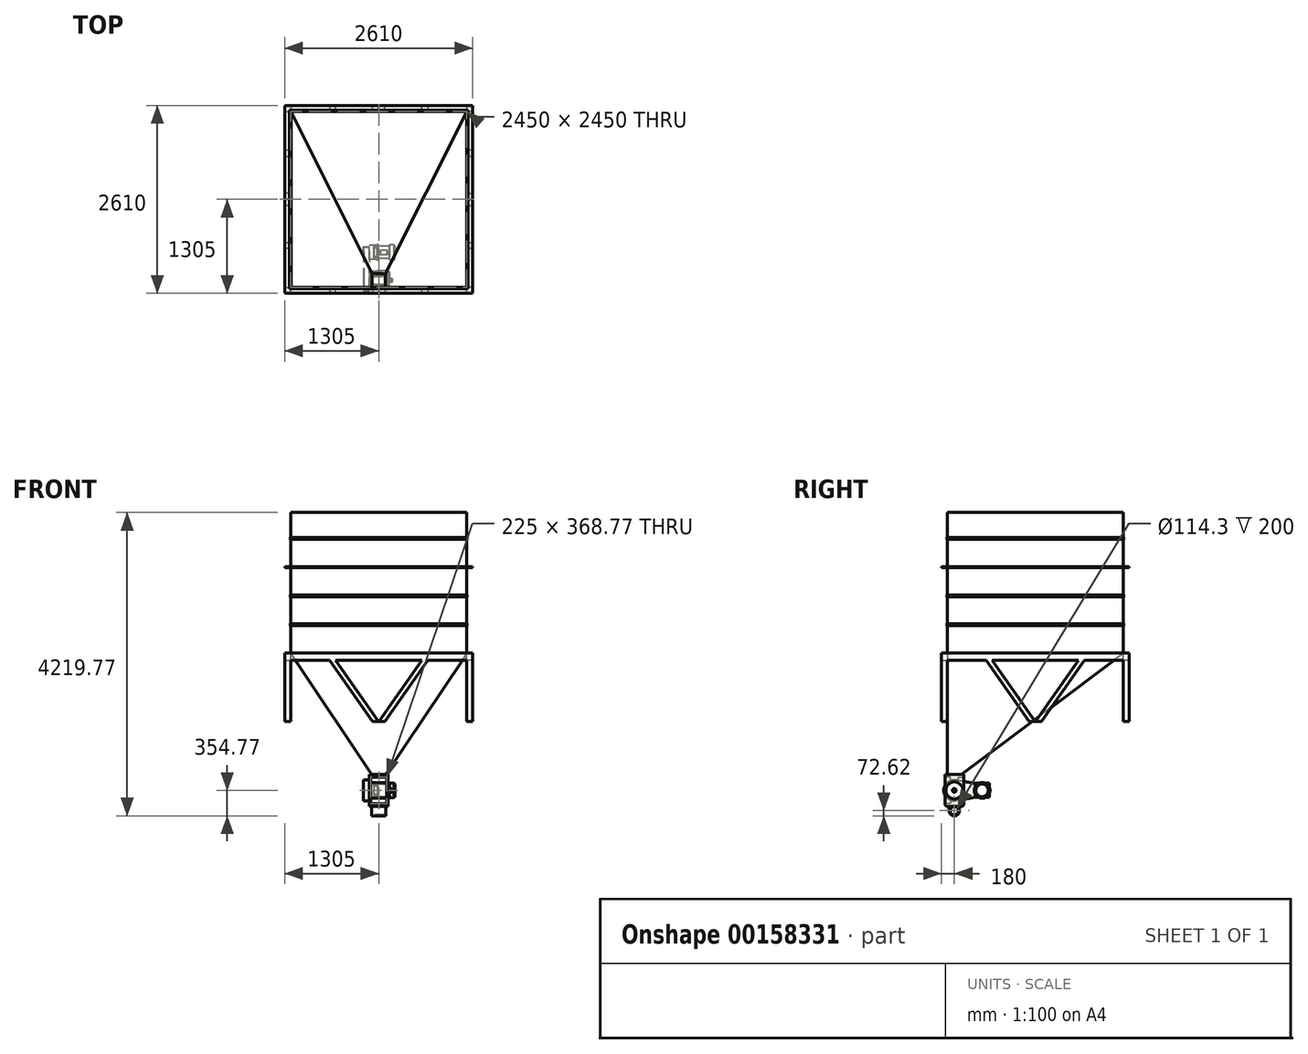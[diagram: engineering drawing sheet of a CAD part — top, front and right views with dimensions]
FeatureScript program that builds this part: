
annotation { "Feature Type Name" : "Feature", "Feature Type Description" : "" }
export const myFeature = defineFeature(function(context is Context, id is Id, definition is map)
    precondition{}
    {
        {
            var Q0;
            Q0=qCreatedBy(makeId("Top.planeOp"),FACE);
            var sketch = newSketch(context, id + "F0", { "sketchPlane" : qUnion([Q0])});
            skLineSegment(sketch, "E0.bottom", {"start": v(-1225, 1225) * mm, "end": v(1225, 1225) * mm});
            skLineSegment(sketch, "E0.top", {"start": v(-1225, -1225) * mm, "end": v(1225, -1225) * mm});
            skLineSegment(sketch, "E0.left", {"start": v(-1225, 1225) * mm, "end": v(-1225, -1225) * mm});
            skLineSegment(sketch, "E0.right", {"start": v(1225, 1225) * mm, "end": v(1225, -1225) * mm});
            skPoint(sketch, "E0.middle", {"position": v(0, 0) * mm});
            skSolve(sketch);
        }
        {
            var Q0;
            Q0=makeQuery(id+"F0.imprint","IMPRINT",FACE,{"disambiguationData":[TD([[makeQuery(id+"F0.imprint","IMPRINT",EDGE,{"derivedFrom":sQuery(id+"F0.wireOp",EDGE,"E0.bottom")}),-1.0]])]});
            extrude(context, id + "F1", {"entities" : qUnion([Q0]), "depth" : 2400 * mm});
        }
        {
            var Q0;
            Q0=makeQuery(id+"F1.opExtrude","CAP_FACE",FACE,{"disambiguationData":[OSD([sQuery(id+"F0.wireOp",EDGE,"E0.bottom"),sQuery(id+"F0.wireOp",EDGE,"E0.top"),sQuery(id+"F0.wireOp",EDGE,"E0.left"),sQuery(id+"F0.wireOp",EDGE,"E0.right")])],"isStart":true});
            cPlane(context, id + "F2", {"entities" : qUnion([Q0]), "cplaneType" : CPlaneType.OFFSET, "offset" : 1680 * mm, "width" : 150 * mm, "height" : 150 * mm});
        }
        {
            var Q0;
            Q0=qCreatedBy(id+"F2.planeOp",FACE);
            var sketch = newSketch(context, id + "F3", { "sketchPlane" : qUnion([Q0])});
            skLineSegment(sketch, "E1.bottom", {"start": v(-100, 1225) * mm, "end": v(100, 1225) * mm});
            skLineSegment(sketch, "E1.top", {"start": v(-100, 1025) * mm, "end": v(100, 1025) * mm});
            skLineSegment(sketch, "E1.left", {"start": v(100, 1225) * mm, "end": v(100, 1025) * mm});
            skLineSegment(sketch, "E1.right", {"start": v(-100, 1225) * mm, "end": v(-100, 1025) * mm});
            skPoint(sketch, "E2", {"position": v(0, 1225) * mm});
            skSolve(sketch);
        }
        {
            var Q1;
            Q1=makeQuery(id+"F1.opExtrude","CAP_FACE",FACE,{"disambiguationData":[OSD([sQuery(id+"F0.wireOp",EDGE,"E0.bottom"),sQuery(id+"F0.wireOp",EDGE,"E0.top"),sQuery(id+"F0.wireOp",EDGE,"E0.left"),sQuery(id+"F0.wireOp",EDGE,"E0.right")])],"isStart":true});
            var Q2;
            Q2=makeQuery(id+"F3.imprint","IMPRINT",FACE,{"disambiguationData":[TD([[makeQuery(id+"F3.imprint","IMPRINT",EDGE,{"derivedFrom":sQuery(id+"F3.wireOp",EDGE,"E1.bottom")}),-1.0]])]});
            loft(context, id + "F4", {"operationType" : NewBodyOperationType.ADD, "sheetProfilesArray" : [{ "sheetProfileEntities" : qUnion([Q1]) }, { "sheetProfileEntities" : qUnion([Q2]) }]});
        }
        {
            var Q0;
            Q0=makeQuery(id+"F1.opExtrude","CAP_FACE",FACE,{"disambiguationData":[OSD([sQuery(id+"F0.wireOp",EDGE,"E0.bottom"),sQuery(id+"F0.wireOp",EDGE,"E0.top"),sQuery(id+"F0.wireOp",EDGE,"E0.left"),sQuery(id+"F0.wireOp",EDGE,"E0.right")])],"isStart":false});
            extrude(context, id + "F5", {"entities" : qUnion([Q0]), "depth" : 400 * mm});
        }
        {
            var Q0;
            Q0=makeQuery(id+"F5.opExtrude","CAP_FACE",FACE,{"disambiguationData":[OSD([sQuery(id+"F0.wireOp",EDGE,"E0.bottom"),sQuery(id+"F0.wireOp",EDGE,"E0.top"),sQuery(id+"F0.wireOp",EDGE,"E0.left"),sQuery(id+"F0.wireOp",EDGE,"E0.right")])],"isStart":false});
            extrude(context, id + "F6", {"entities" : qUnion([Q0]), "depth" : 400 * mm});
        }
        {
            var Q0;
            Q0=makeQuery(id+"F1.opExtrude","CAP_FACE",FACE,{"disambiguationData":[OSD([sQuery(id+"F0.wireOp",EDGE,"E0.bottom"),sQuery(id+"F0.wireOp",EDGE,"E0.top"),sQuery(id+"F0.wireOp",EDGE,"E0.left"),sQuery(id+"F0.wireOp",EDGE,"E0.right")])],"isStart":false});
            var Q1;
            Q1=makeQuery(id+"F4.opLoft","CAP_FACE",FACE,{"disambiguationData":[OSD([makeQuery(id+"F3.imprint","IMPRINT",FACE,{"disambiguationData":[TD([[makeQuery(id+"F3.imprint","IMPRINT",EDGE,{"derivedFrom":sQuery(id+"F3.wireOp",EDGE,"E1.bottom")}),-1.0]])]})])],"isStart":true});
            shell(context, id + "F7", {"entities" : qUnion([Q0, Q1]), "thickness" : 5 * mm});
        }
        {
            var Q0;
            Q0=makeQuery(id+"F1.opExtrude","CAP_FACE",FACE,{"disambiguationData":[OSD([sQuery(id+"F0.wireOp",EDGE,"E0.bottom"),sQuery(id+"F0.wireOp",EDGE,"E0.top"),sQuery(id+"F0.wireOp",EDGE,"E0.left"),sQuery(id+"F0.wireOp",EDGE,"E0.right")])],"isStart":false});
            cPlane(context, id + "F8", {"entities" : qUnion([Q0]), "cplaneType" : CPlaneType.OFFSET, "offset" : 1200 * mm, "oppositeDirection" : true, "width" : 150 * mm, "height" : 150 * mm});
        }
        {
            var Q0;
            Q0=qCreatedBy(id+"F8.planeOp",FACE);
            var sketch = newSketch(context, id + "F9", { "sketchPlane" : qUnion([Q0])});
            skLineSegment(sketch, "E3.bottom", {"start": v(-1305, 1305) * mm, "end": v(1305, 1305) * mm});
            skLineSegment(sketch, "E3.top", {"start": v(-1305, -1305) * mm, "end": v(1305, -1305) * mm});
            skLineSegment(sketch, "E3.left", {"start": v(-1305, 1305) * mm, "end": v(-1305, -1305) * mm});
            skLineSegment(sketch, "E3.right", {"start": v(1305, 1305) * mm, "end": v(1305, -1305) * mm});
            skPoint(sketch, "E3.middle", {"position": v(0, 0) * mm});
            skLineSegment(sketch, "E4.0", {"start": v(-1225, 1225) * mm, "end": v(-1225, -1225) * mm});
            skLineSegment(sketch, "E4.1", {"start": v(-1225, 1225) * mm, "end": v(1225, 1225) * mm});
            skLineSegment(sketch, "E4.2", {"start": v(1225, 1225) * mm, "end": v(1225, -1225) * mm});
            skLineSegment(sketch, "E4.3", {"start": v(-1225, -1225) * mm, "end": v(1225, -1225) * mm});
            skSolve(sketch);
        }
        {
            var Q0;
            Q0=qSketchRegion(id+"F9",true);
            extrude(context, id + "F10", {"entities" : qUnion([Q0]), "endBound" : BoundingType.SYMMETRIC, "depth" : 10 * mm});
        }
        {
            var Q0;
            {var subQ0=sQuery(id+"F0.wireOp",EDGE,"E0.right");var subQ1=sQuery(id+"F0.wireOp",EDGE,"E0.left");var subQ2=sQuery(id+"F0.wireOp",EDGE,"E0.bottom");Q0=makeQuery(id+"F10.boolean.opBoolean","SPLIT",FACE,{"disambiguationData":[TD([makeQuery(id+"F1.opExtrude","CAP_FACE",FACE,{"disambiguationData":[OSD([subQ2,sQuery(id+"F0.wireOp",EDGE,"E0.top"),subQ1,subQ0])],"isStart":false})])],"derivedFrom":makeQuery(id+"F1.opExtrude","SWEPT_FACE",FACE,{"disambiguationData":[OSD([subQ2])]})});}
            var sketch = newSketch(context, id + "F11", { "sketchPlane" : qUnion([Q0])});
            skLineSegment(sketch, "E5", {"start": v(-1225, 2014.14) * mm, "end": v(-1239.14, 2000) * mm});
            skLineSegment(sketch, "E6", {"start": v(-1239.14, 2000) * mm, "end": v(-1225, 1985.86) * mm});
            skLineSegment(sketch, "E7", {"start": v(-1225, 1985.86) * mm, "end": v(-1225, 2014.14) * mm});
            skPoint(sketch, "E8", {"position": v(-1225, 2000) * mm});
            skSolve(sketch);
        }
        {
            var Q0;
            Q0=makeQuery(id+"F1.opExtrude","CAP_FACE",FACE,{"disambiguationData":[OSD([sQuery(id+"F0.wireOp",EDGE,"E0.bottom"),sQuery(id+"F0.wireOp",EDGE,"E0.top"),sQuery(id+"F0.wireOp",EDGE,"E0.left"),sQuery(id+"F0.wireOp",EDGE,"E0.right")])],"isStart":false});
            var Q1;
            Q1=sQuery(id+"F11.wireOp",VERTEX,"E8");
            cPlane(context, id + "F12", {"entities" : qUnion([Q0, Q1]), "cplaneType" : CPlaneType.PLANE_POINT, "offset" : 25 * mm, "width" : 150 * mm, "height" : 150 * mm});
        }
        {
            var Q0;
            Q0=qCreatedBy(id+"F12.planeOp",FACE);
            var sketch = newSketch(context, id + "F13", { "sketchPlane" : qUnion([Q0])});
            skLineSegment(sketch, "E9.0.0", {"start": v(1225, 1225) * mm, "end": v(-1225, 1225) * mm});
            skLineSegment(sketch, "E9.0.1", {"start": v(-1225, 1225) * mm, "end": v(-1225, -1225) * mm});
            skLineSegment(sketch, "E9.0.2", {"start": v(-1225, -1225) * mm, "end": v(1225, -1225) * mm});
            skLineSegment(sketch, "E9.0.3", {"start": v(1225, -1225) * mm, "end": v(1225, 1225) * mm});
            skSolve(sketch);
        }
        {
            var Q0;
            Q0=qSketchRegion(id+"F11",true);
            var Q1;
            Q1=qConstructionFilter(qBodyType(qCreatedBy(id+"F13",EDGE),BodyType.WIRE),ConstructionObject.NO);
            sweep(context, id + "F14", {"profiles" : qUnion([Q0]), "path" : qUnion([Q1])});
        }
        {
            var Q0;
            Q0=makeQuery(id+"F1.opExtrude","CAP_FACE",FACE,{"disambiguationData":[OSD([sQuery(id+"F0.wireOp",EDGE,"E0.bottom"),sQuery(id+"F0.wireOp",EDGE,"E0.top"),sQuery(id+"F0.wireOp",EDGE,"E0.left"),sQuery(id+"F0.wireOp",EDGE,"E0.right")])],"isStart":false});
            cPlane(context, id + "F15", {"entities" : qUnion([Q0]), "cplaneType" : CPlaneType.OFFSET, "offset" : 600 * mm, "oppositeDirection" : true, "width" : 150 * mm, "height" : 150 * mm});
        }
        {
            var Q0;
            Q0=makeQuery(id+"F14.opSweep","SWEPT_BODY",BODY,{"disambiguationData":[OSD([sQuery(id+"F11.wireOp",EDGE,"E5"),sQuery(id+"F11.wireOp",EDGE,"E6"),sQuery(id+"F11.wireOp",EDGE,"E7"),sQuery(id+"F13.wireOp",EDGE,"E9.0.3")])]});
            var Q1;
            Q1=qCreatedBy(id+"F15.planeOp",FACE);
            mirror(context, id + "F16", {"entities" : qUnion([Q0]), "mirrorPlane" : qUnion([Q1])});
        }
        {
            var Q0;
            Q0=makeQuery(id+"F16.opPattern","COPY",BODY,{"derivedFrom":makeQuery(id+"F14.opSweep","SWEPT_BODY",BODY,{"disambiguationData":[OSD([sQuery(id+"F11.wireOp",EDGE,"E5"),sQuery(id+"F11.wireOp",EDGE,"E6"),sQuery(id+"F11.wireOp",EDGE,"E7"),sQuery(id+"F13.wireOp",EDGE,"E9.0.3")])]}),"instanceName":"1"});
            var Q1;
            Q1=makeQuery(id+"F14.opSweep","SWEPT_BODY",BODY,{"disambiguationData":[OSD([sQuery(id+"F11.wireOp",EDGE,"E5"),sQuery(id+"F11.wireOp",EDGE,"E6"),sQuery(id+"F11.wireOp",EDGE,"E7"),sQuery(id+"F13.wireOp",EDGE,"E9.0.3")])]});
            var Q2;
            Q2=qCreatedBy(id+"F8.planeOp",FACE);
            mirror(context, id + "F17", {"operationType" : NewBodyOperationType.ADD, "entities" : qUnion([Q0, Q1]), "mirrorPlane" : qUnion([Q2])});
        }
        {
            var Q0;
            Q0=makeQuery(id+"F1.opExtrude","CAP_FACE",FACE,{"disambiguationData":[OSD([sQuery(id+"F0.wireOp",EDGE,"E0.bottom"),sQuery(id+"F0.wireOp",EDGE,"E0.top"),sQuery(id+"F0.wireOp",EDGE,"E0.left"),sQuery(id+"F0.wireOp",EDGE,"E0.right")])],"isStart":false});
            cPlane(context, id + "F18", {"entities" : qUnion([Q0]), "cplaneType" : CPlaneType.OFFSET, "offset" : 1800 * mm, "oppositeDirection" : true, "width" : 150 * mm, "height" : 150 * mm});
        }
        {
            var Q0;
            Q0=makeQuery(id+"F10.opExtrude","SWEPT_BODY",BODY,{"disambiguationData":[OSD([sQuery(id+"F9.wireOp",EDGE,"E3.bottom"),sQuery(id+"F9.wireOp",EDGE,"E3.top"),sQuery(id+"F9.wireOp",EDGE,"E3.left"),sQuery(id+"F9.wireOp",EDGE,"E3.right")])]});
            var Q1;
            Q1=qCreatedBy(id+"F18.planeOp",FACE);
            mirror(context, id + "F19", {"entities" : qUnion([Q0]), "mirrorPlane" : qUnion([Q1])});
        }
        {
            var Q0;
            Q0=makeQuery(id+"F5.opExtrude","SWEPT_BODY",BODY,{"disambiguationData":[OSD([sQuery(id+"F0.wireOp",EDGE,"E0.bottom"),sQuery(id+"F0.wireOp",EDGE,"E0.top"),sQuery(id+"F0.wireOp",EDGE,"E0.left"),sQuery(id+"F0.wireOp",EDGE,"E0.right")])]});
            var Q1;
            Q1=makeQuery(id+"F6.opExtrude","SWEPT_BODY",BODY,{"disambiguationData":[OSD([sQuery(id+"F0.wireOp",EDGE,"E0.bottom"),sQuery(id+"F0.wireOp",EDGE,"E0.top"),sQuery(id+"F0.wireOp",EDGE,"E0.left"),sQuery(id+"F0.wireOp",EDGE,"E0.right")])]});
            deleteBodies(context, id + "F20", {"entities" : qUnion([Q0, Q1])});
        }
        {
            var Q0;
            Q0=makeQuery(id+"F1.opExtrude","CAP_FACE",FACE,{"disambiguationData":[OSD([sQuery(id+"F0.wireOp",EDGE,"E0.bottom"),sQuery(id+"F0.wireOp",EDGE,"E0.top"),sQuery(id+"F0.wireOp",EDGE,"E0.left"),sQuery(id+"F0.wireOp",EDGE,"E0.right")])],"isStart":false});
            var sketch = newSketch(context, id + "F21", { "sketchPlane" : qUnion([Q0])});
            skLineSegment(sketch, "E10.bottom", {"start": v(-1536.15, 1536.15) * mm, "end": v(1536.15, 1536.15) * mm});
            skLineSegment(sketch, "E10.top", {"start": v(-1536.15, -1536.15) * mm, "end": v(1536.15, -1536.15) * mm});
            skLineSegment(sketch, "E10.left", {"start": v(-1536.15, 1536.15) * mm, "end": v(-1536.15, -1536.15) * mm});
            skLineSegment(sketch, "E10.right", {"start": v(1536.15, 1536.15) * mm, "end": v(1536.15, -1536.15) * mm});
            skPoint(sketch, "E10.middle", {"position": v(0, 0) * mm});
            skSolve(sketch);
        }
        {
            var Q0;
            Q0=qSketchRegion(id+"F21",true);
            extrude(context, id + "F22", {"entities" : qUnion([Q0]), "operationType" : NewBodyOperationType.REMOVE, "oppositeDirection" : true, "depth" : 440 * mm});
        }
        {
            var Q0;
            Q0=makeQuery(id+"F4.opLoft","CAP_FACE",FACE,{"disambiguationData":[OSD([makeQuery(id+"F3.imprint","IMPRINT",FACE,{"disambiguationData":[TD([[makeQuery(id+"F3.imprint","IMPRINT",EDGE,{"derivedFrom":sQuery(id+"F3.wireOp",EDGE,"E1.bottom")}),-1.0]])]})])],"isStart":true});
            var sketch = newSketch(context, id + "F23", { "sketchPlane" : qUnion([Q0])});
            skLineSegment(sketch, "E11.0", {"start": v(-130, 1255) * mm, "end": v(-130, 995) * mm});
            skLineSegment(sketch, "E11.1", {"start": v(130, 1255) * mm, "end": v(-130, 1255) * mm});
            skLineSegment(sketch, "E11.2", {"start": v(130, 995) * mm, "end": v(130, 1255) * mm});
            skLineSegment(sketch, "E11.3", {"start": v(-130, 995) * mm, "end": v(130, 995) * mm});
            skSolve(sketch);
        }
        {
            var Q0;
            Q0=qSketchRegion(id+"F23",true);
            extrude(context, id + "F24", {"entities" : qUnion([Q0]), "depth" : 450 * mm});
        }
        {
            var Q0;
            Q0=makeQuery(id+"F24.opExtrude","SWEPT_FACE",FACE,{"disambiguationData":[OSD([sQuery(id+"F23.wireOp",EDGE,"E11.2")])]});
            var sketch = newSketch(context, id + "F25", { "sketchPlane" : qUnion([Q0])});
            skCircle(sketch, "E12", {"center": v(-1125, -1905) * mm, "radius": 118.36 * mm});
            skPoint(sketch, "E13", {"position": v(-1255, -1905) * mm});
            skPoint(sketch, "E14", {"position": v(-1125, -1680) * mm});
            skSolve(sketch);
        }
        {
            var Q0;
            Q0=qSketchRegion(id+"F25",true);
            extrude(context, id + "F26", {"entities" : qUnion([Q0]), "operationType" : NewBodyOperationType.ADD, "depth" : 17.5 * mm});
        }
        {
            var Q0;
            Q0=makeQuery(id+"F26.opExtrude","CAP_FACE",FACE,{"disambiguationData":[OSD([sQuery(id+"F25.wireOp",EDGE,"E12")])],"isStart":false});
            var sketch = newSketch(context, id + "F27", { "sketchPlane" : qUnion([Q0])});
            skCircle(sketch, "E15", {"center": v(-1125, -1905) * mm, "radius": 25.57 * mm});
            skSolve(sketch);
        }
        {
            var Q0;
            Q0=qSketchRegion(id+"F27",true);
            extrude(context, id + "F28", {"entities" : qUnion([Q0]), "operationType" : NewBodyOperationType.ADD, "depth" : 40 * mm});
        }
        {
            var Q0;
            Q0=makeQuery(id+"F28.opExtrude","CAP_EDGE",EDGE,{"disambiguationData":[OSD([sQuery(id+"F27.wireOp",EDGE,"E15")])],"isStart":false});
            chamfer(context, id + "F29", {"entities" : qUnion([Q0]), "width" : 5 * mm, "tangentPropagation" : true});
        }
        {
            var Q0;
            Q0=qCreatedBy(makeId("Right.planeOp"),FACE);
            var sketch = newSketch(context, id + "F30", { "sketchPlane" : qUnion([Q0])});
            skArc(sketch, "E16", {"start": v(-1177.5, -1798.91) * mm, "mid": v(-1243.36, -1905) * mm, "end": v(-1177.5, -2011.09) * mm});
            skLineSegment(sketch, "E17", {"start": v(-1125, -1680) * mm, "end": v(-1125, -2130) * mm, "construction": true});
            skArc(sketch, "E18.MirrorCS", {"start": v(-1072.5, -1798.91) * mm, "mid": v(-1006.64, -1905) * mm, "end": v(-1072.5, -2011.09) * mm});
            skLineSegment(sketch, "E19", {"start": v(-1177.5, -1798.91) * mm, "end": v(-1177.5, -1720.61) * mm});
            skLineSegment(sketch, "E20", {"start": v(-1255, -1905) * mm, "end": v(-995, -1905) * mm, "construction": true});
            skLineSegment(sketch, "E21", {"start": v(-1177.5, -1720.61) * mm, "end": v(-1255, -1720.61) * mm});
            skLineSegment(sketch, "E22", {"start": v(-1255, -1720.61) * mm, "end": v(-1255, -1905) * mm});
            skLineSegment(sketch, "E23.MirrorCS", {"start": v(-1072.5, -1798.91) * mm, "end": v(-1072.5, -1720.61) * mm});
            skLineSegment(sketch, "E24.MirrorCS", {"start": v(-1072.5, -1720.61) * mm, "end": v(-995, -1720.61) * mm});
            skLineSegment(sketch, "E25.MirrorCS", {"start": v(-995, -1720.61) * mm, "end": v(-995, -1905) * mm});
            skLineSegment(sketch, "E26.MirrorCS", {"start": v(-995, -2089.39) * mm, "end": v(-995, -1905) * mm});
            skLineSegment(sketch, "E27.MirrorCS", {"start": v(-1072.5, -2089.39) * mm, "end": v(-995, -2089.39) * mm});
            skLineSegment(sketch, "E28.MirrorCS", {"start": v(-1072.5, -2011.09) * mm, "end": v(-1072.5, -2089.39) * mm});
            skLineSegment(sketch, "E29.MirrorCS", {"start": v(-1177.5, -2011.09) * mm, "end": v(-1177.5, -2089.39) * mm});
            skLineSegment(sketch, "E30.MirrorCS", {"start": v(-1177.5, -2089.39) * mm, "end": v(-1255, -2089.39) * mm});
            skLineSegment(sketch, "E31.MirrorCS", {"start": v(-1255, -2089.39) * mm, "end": v(-1255, -1905) * mm});
            skSolve(sketch);
        }
        {
            var Q0;
            Q0=qSketchRegion(id+"F30",true);
            extrude(context, id + "F31", {"entities" : qUnion([Q0]), "operationType" : NewBodyOperationType.REMOVE, "endBound" : BoundingType.SYMMETRIC, "oppositeDirection" : true, "depth" : 225 * mm});
        }
        {
            var Q0;
            Q0=makeQuery(id+"F24.opExtrude","SWEPT_FACE",FACE,{"disambiguationData":[OSD([sQuery(id+"F23.wireOp",EDGE,"E11.0")])]});
            var sketch = newSketch(context, id + "F32", { "sketchPlane" : qUnion([Q0])});
            skLineSegment(sketch, "E32", {"start": v(724.05, -1826.48) * mm, "end": v(1099.3, -1759.97) * mm});
            skLineSegment(sketch, "E33", {"start": v(724.05, -1983.52) * mm, "end": v(1099.3, -2050.03) * mm});
            skArc(sketch, "E34", {"start": v(724.05, -1826.48) * mm, "mid": v(658.22, -1905) * mm, "end": v(724.05, -1983.52) * mm});
            skArc(sketch, "E35", {"start": v(724.05, -1983.52) * mm, "mid": v(817.7, -1905) * mm, "end": v(724.05, -1826.48) * mm, "construction": true});
            skArc(sketch, "E36", {"start": v(1099.3, -1759.97) * mm, "mid": v(977.7, -1905) * mm, "end": v(1099.3, -2050.03) * mm, "construction": true});
            skArc(sketch, "E37", {"start": v(1099.3, -2050.03) * mm, "mid": v(1272.3, -1905) * mm, "end": v(1099.3, -1759.97) * mm});
            skSolve(sketch);
        }
        {
            var Q0;
            Q0=qSketchRegion(id+"F32",true);
            extrude(context, id + "F33", {"entities" : qUnion([Q0]), "depth" : 85 * mm});
        }
        {
            var Q0;
            Q0=makeQuery(id+"F33.opExtrude","CAP_FACE",FACE,{"disambiguationData":[OSD([sQuery(id+"F32.wireOp",EDGE,"E32"),sQuery(id+"F32.wireOp",EDGE,"E33"),sQuery(id+"F32.wireOp",EDGE,"E34"),sQuery(id+"F32.wireOp",EDGE,"E37")])],"isStart":true});
            shell(context, id + "F34", {"entities" : qUnion([Q0]), "thickness" : 5 * mm});
        }
        {
            var Q0;
            Q0=makeQuery(id+"F33.opExtrude","CAP_FACE",FACE,{"disambiguationData":[OSD([sQuery(id+"F32.wireOp",EDGE,"E32"),sQuery(id+"F32.wireOp",EDGE,"E33"),sQuery(id+"F32.wireOp",EDGE,"E34"),sQuery(id+"F32.wireOp",EDGE,"E37")])],"isStart":true});
            var sketch = newSketch(context, id + "F35", { "sketchPlane" : qUnion([Q0])});
            skLineSegment(sketch, "E38.bottom", {"start": v(-836.4, -1806.57) * mm, "end": v(-639.53, -1806.57) * mm});
            skLineSegment(sketch, "E38.top", {"start": v(-836.4, -2003.43) * mm, "end": v(-639.53, -2003.43) * mm});
            skLineSegment(sketch, "E38.left", {"start": v(-836.4, -1806.57) * mm, "end": v(-836.4, -2003.43) * mm});
            skLineSegment(sketch, "E38.right", {"start": v(-639.53, -1806.57) * mm, "end": v(-639.53, -2003.43) * mm});
            skPoint(sketch, "E38.middle", {"position": v(-737.97, -1905) * mm});
            skSolve(sketch);
        }
        {
            var Q0;
            Q0=qSketchRegion(id+"F35",true);
            extrude(context, id + "F36", {"entities" : qUnion([Q0]), "depth" : 60 * mm});
        }
        {
            var Q0;
            Q0=makeQuery(id+"F36.opExtrude","CAP_FACE",FACE,{"disambiguationData":[OSD([sQuery(id+"F35.wireOp",EDGE,"E38.bottom"),sQuery(id+"F35.wireOp",EDGE,"E38.top"),sQuery(id+"F35.wireOp",EDGE,"E38.left"),sQuery(id+"F35.wireOp",EDGE,"E38.right")])],"isStart":false});
            var sketch = newSketch(context, id + "F37", { "sketchPlane" : qUnion([Q0])});
            skArc(sketch, "E39", {"start": v(-817, -1846.33) * mm, "mid": v(-836.4, -1905) * mm, "end": v(-817, -1963.67) * mm});
            skLineSegment(sketch, "E40", {"start": v(-679.3, -1825.97) * mm, "end": v(-658.76, -1813.38) * mm});
            skLineSegment(sketch, "E41", {"start": v(-737.97, -1905) * mm, "end": v(-639.53, -1806.57) * mm, "construction": true});
            skLineSegment(sketch, "E42", {"start": v(-658.76, -1813.38) * mm, "end": v(-652.56, -1819.59) * mm});
            skLineSegment(sketch, "E43.MirrorCS", {"start": v(-646.35, -1825.8) * mm, "end": v(-652.56, -1819.59) * mm});
            skLineSegment(sketch, "E44.MirrorCS", {"start": v(-658.93, -1846.33) * mm, "end": v(-646.35, -1825.8) * mm});
            skLineSegment(sketch, "E45", {"start": v(-737.97, -1806.57) * mm, "end": v(-737.97, -2003.43) * mm, "construction": true});
            skLineSegment(sketch, "E46", {"start": v(-639.53, -1905) * mm, "end": v(-836.4, -1905) * mm, "construction": true});
            skLineSegment(sketch, "E47.MirrorCS", {"start": v(-796.64, -1825.97) * mm, "end": v(-817.17, -1813.38) * mm});
            skLineSegment(sketch, "E48.MirrorCS", {"start": v(-817, -1846.33) * mm, "end": v(-829.58, -1825.8) * mm});
            skLineSegment(sketch, "E49.MirrorCS", {"start": v(-829.58, -1825.8) * mm, "end": v(-823.38, -1819.59) * mm});
            skLineSegment(sketch, "E50.MirrorCS", {"start": v(-817.17, -1813.38) * mm, "end": v(-823.38, -1819.59) * mm});
            skLineSegment(sketch, "E51.MirrorCS", {"start": v(-658.93, -1963.67) * mm, "end": v(-646.35, -1984.2) * mm});
            skLineSegment(sketch, "E52.MirrorCS", {"start": v(-658.76, -1996.62) * mm, "end": v(-652.56, -1990.41) * mm});
            skLineSegment(sketch, "E53.MirrorCS", {"start": v(-679.3, -1984.03) * mm, "end": v(-658.76, -1996.62) * mm});
            skLineSegment(sketch, "E54.MirrorCS", {"start": v(-796.64, -1984.03) * mm, "end": v(-817.17, -1996.62) * mm});
            skLineSegment(sketch, "E55.MirrorCS", {"start": v(-817.17, -1996.62) * mm, "end": v(-823.38, -1990.41) * mm});
            skLineSegment(sketch, "E56.MirrorCS", {"start": v(-829.58, -1984.2) * mm, "end": v(-823.38, -1990.41) * mm});
            skLineSegment(sketch, "E57.MirrorCS", {"start": v(-817, -1963.67) * mm, "end": v(-829.58, -1984.2) * mm});
            skLineSegment(sketch, "E58.MirrorCS", {"start": v(-646.35, -1984.2) * mm, "end": v(-652.56, -1990.41) * mm});
            skArc(sketch, "E59.trimOffspring", {"start": v(-679.3, -1825.97) * mm, "mid": v(-737.97, -1806.57) * mm, "end": v(-796.64, -1825.97) * mm});
            skArc(sketch, "E60.trimOffspring", {"start": v(-658.93, -1963.67) * mm, "mid": v(-639.53, -1905) * mm, "end": v(-658.93, -1846.33) * mm});
            skArc(sketch, "E61.trimOffspring", {"start": v(-796.64, -1984.03) * mm, "mid": v(-737.97, -2003.43) * mm, "end": v(-679.3, -1984.03) * mm});
            skSolve(sketch);
        }
        {
            var Q0;
            Q0=qSketchRegion(id+"F37",true);
            extrude(context, id + "F38", {"entities" : qUnion([Q0]), "operationType" : NewBodyOperationType.ADD, "depth" : 50 * mm});
        }
        {
            var Q0;
            Q0=makeQuery(id+"F38.opExtrude","CAP_FACE",FACE,{"disambiguationData":[OSD([sQuery(id+"F37.wireOp",EDGE,"E39"),sQuery(id+"F37.wireOp",EDGE,"E40"),sQuery(id+"F37.wireOp",EDGE,"E42"),sQuery(id+"F37.wireOp",EDGE,"E43.MirrorCS"),sQuery(id+"F37.wireOp",EDGE,"E44.MirrorCS"),sQuery(id+"F37.wireOp",EDGE,"E47.MirrorCS"),sQuery(id+"F37.wireOp",EDGE,"E48.MirrorCS"),sQuery(id+"F37.wireOp",EDGE,"E49.MirrorCS"),sQuery(id+"F37.wireOp",EDGE,"E50.MirrorCS"),sQuery(id+"F37.wireOp",EDGE,"E51.MirrorCS"),sQuery(id+"F37.wireOp",EDGE,"E52.MirrorCS"),sQuery(id+"F37.wireOp",EDGE,"E53.MirrorCS"),sQuery(id+"F37.wireOp",EDGE,"E54.MirrorCS"),sQuery(id+"F37.wireOp",EDGE,"E55.MirrorCS"),sQuery(id+"F37.wireOp",EDGE,"E56.MirrorCS"),sQuery(id+"F37.wireOp",EDGE,"E57.MirrorCS"),sQuery(id+"F37.wireOp",EDGE,"E58.MirrorCS"),sQuery(id+"F37.wireOp",EDGE,"E59.trimOffspring"),sQuery(id+"F37.wireOp",EDGE,"E60.trimOffspring"),sQuery(id+"F37.wireOp",EDGE,"E61.trimOffspring")])],"isStart":false});
            var sketch = newSketch(context, id + "F39", { "sketchPlane" : qUnion([Q0])});
            skCircle(sketch, "E62", {"center": v(-737.97, -1905) * mm, "radius": 110.24 * mm});
            skSolve(sketch);
        }
        {
            var Q0;
            Q0=qSketchRegion(id+"F39",true);
            extrude(context, id + "F40", {"entities" : qUnion([Q0]), "operationType" : NewBodyOperationType.ADD, "depth" : 7.5 * mm});
        }
        {
            var Q0;
            Q0=makeQuery(id+"F40.opExtrude","CAP_FACE",FACE,{"disambiguationData":[OSD([sQuery(id+"F39.wireOp",EDGE,"E62")])],"isStart":false});
            var sketch = newSketch(context, id + "F41", { "sketchPlane" : qUnion([Q0])});
            skCircle(sketch, "E63", {"center": v(-737.97, -1905) * mm, "radius": 86.74 * mm});
            skSolve(sketch);
        }
        {
            var Q0;
            Q0=qSketchRegion(id+"F41",true);
            extrude(context, id + "F42", {"entities" : qUnion([Q0]), "operationType" : NewBodyOperationType.ADD, "depth" : 160 * mm});
        }
        {
            var Q0;
            Q0=makeQuery(id+"F42.opExtrude","CAP_FACE",FACE,{"disambiguationData":[OSD([sQuery(id+"F41.wireOp",EDGE,"E63")])],"isStart":false});
            var sketch = newSketch(context, id + "F43", { "sketchPlane" : qUnion([Q0])});
            skCircle(sketch, "E64", {"center": v(-737.97, -1905) * mm, "radius": 103.35 * mm});
            skSolve(sketch);
        }
        {
            var Q0;
            Q0=qSketchRegion(id+"F43",true);
            extrude(context, id + "F44", {"entities" : qUnion([Q0]), "operationType" : NewBodyOperationType.ADD, "depth" : 77.5 * mm});
        }
        {
            var Q0;
            Q0=makeQuery(id+"F44.opExtrude","CAP_EDGE",EDGE,{"disambiguationData":[OSD([sQuery(id+"F43.wireOp",EDGE,"E64")])],"isStart":false});
            chamfer(context, id + "F45", {"entities" : qUnion([Q0]), "width" : 15 * mm, "tangentPropagation" : true});
        }
        {
            var Q0;
            Q0=makeQuery(id+"F36.opExtrude","SWEPT_FACE",FACE,{"disambiguationData":[OSD([sQuery(id+"F35.wireOp",EDGE,"E38.bottom")])]});
            var sketch = newSketch(context, id + "F46", { "sketchPlane" : qUnion([Q0])});
            skLineSegment(sketch, "E65.bottom", {"start": v(115.81, -707.31) * mm, "end": v(22.17, -707.31) * mm});
            skLineSegment(sketch, "E65.top", {"start": v(115.81, -768.62) * mm, "end": v(22.17, -768.62) * mm});
            skLineSegment(sketch, "E65.left", {"start": v(115.81, -707.31) * mm, "end": v(115.81, -768.62) * mm});
            skLineSegment(sketch, "E65.right", {"start": v(22.17, -707.31) * mm, "end": v(22.17, -768.62) * mm});
            skPoint(sketch, "E65.middle", {"position": v(68.99, -737.97) * mm});
            skPoint(sketch, "E66", {"position": v(-130, -737.97) * mm});
            skSolve(sketch);
        }
        {
            var Q0;
            Q0=qSketchRegion(id+"F46",true);
            extrude(context, id + "F47", {"entities" : qUnion([Q0]), "operationType" : NewBodyOperationType.ADD, "endBound" : BoundingType.UP_TO_NEXT, "oppositeDirection" : true, "depth" : 25 * mm});
        }
        {
            var Q0;
            Q0=qCreatedBy(makeId("Right.planeOp"),FACE);
            var sketch = newSketch(context, id + "F48", { "sketchPlane" : qUnion([Q0])});
            skCircle(sketch, "E67", {"center": v(-1125, -2187.15) * mm, "radius": 57.15 * mm});
            skCircle(sketch, "E68.0", {"center": v(-1125, -1905) * mm, "radius": 118.36 * mm, "construction": true});
            skArc(sketch, "E69", {"start": v(-1195.78, -2170.89) * mm, "mid": v(-1125, -2259.77) * mm, "end": v(-1054.22, -2170.89) * mm});
            skArc(sketch, "E70", {"start": v(-1021.67, -2130) * mm, "mid": v(-1047.8, -2142.6) * mm, "end": v(-1054.22, -2170.89) * mm});
            skArc(sketch, "E71", {"start": v(-1195.78, -2170.89) * mm, "mid": v(-1202.2, -2142.6) * mm, "end": v(-1228.33, -2130) * mm});
            skLineSegment(sketch, "E72", {"start": v(-1228.33, -2163.4) * mm, "end": v(-1021.67, -2163.4) * mm, "construction": true});
            skLineSegment(sketch, "E73", {"start": v(-1228.33, -2130) * mm, "end": v(-1228.33, -2117.94) * mm});
            skLineSegment(sketch, "E74", {"start": v(-1228.33, -2117.94) * mm, "end": v(-1021.67, -2117.94) * mm});
            skLineSegment(sketch, "E75", {"start": v(-1021.67, -2117.94) * mm, "end": v(-1021.67, -2130) * mm});
            skSolve(sketch);
        }
        {
            var Q0;
            {var subQ3=sQuery(id+"F48.wireOp",EDGE,"E67");Q0=makeQuery(id+"F48.imprint","IMPRINT",FACE,{"disambiguationData":[TD([[makeQuery(id+"F48.imprint","IMPRINT",EDGE,{"derivedFrom":subQ3}),-1.0]])]});}
            extrude(context, id + "F49", {"entities" : qUnion([Q0]), "operationType" : NewBodyOperationType.ADD, "endBound" : BoundingType.SYMMETRIC, "depth" : 200 * mm});
        }
        {
            var Q0;
            Q0=makeQuery(id+"F24.opExtrude","CAP_EDGE",EDGE,{"disambiguationData":[OSD([sQuery(id+"F23.wireOp",EDGE,"E11.3")])],"isStart":false});
            var Q1;
            Q1=makeQuery(id+"F24.opExtrude","CAP_EDGE",EDGE,{"disambiguationData":[OSD([sQuery(id+"F23.wireOp",EDGE,"E11.1")])],"isStart":false});
            chamfer(context, id + "F50", {"entities" : qUnion([Q0, Q1]), "width" : 20 * mm, "tangentPropagation" : true});
        }
        {
            var Q0;
            Q0=makeQuery(id+"F19.opPattern","COPY",FACE,{"derivedFrom":makeQuery(id+"F10.opExtrude","CAP_FACE",FACE,{"disambiguationData":[OSD([sQuery(id+"F9.wireOp",EDGE,"E3.bottom"),sQuery(id+"F9.wireOp",EDGE,"E3.top"),sQuery(id+"F9.wireOp",EDGE,"E3.left"),sQuery(id+"F9.wireOp",EDGE,"E3.right"),sQuery(id+"F9.wireOp",EDGE,"E4.0"),sQuery(id+"F9.wireOp",EDGE,"E4.1"),sQuery(id+"F9.wireOp",EDGE,"E4.2"),sQuery(id+"F9.wireOp",EDGE,"E4.3")])],"isStart":false}),"instanceName":"1"});
            var sketch = newSketch(context, id + "F51", { "sketchPlane" : qUnion([Q0])});
            skLineSegment(sketch, "E76.bottom", {"start": v(-1305, 1305) * mm, "end": v(-1225, 1305) * mm});
            skLineSegment(sketch, "E76.top", {"start": v(-1305, 1225) * mm, "end": v(-1225, 1225) * mm});
            skLineSegment(sketch, "E76.left", {"start": v(-1305, 1305) * mm, "end": v(-1305, 1225) * mm});
            skLineSegment(sketch, "E76.right", {"start": v(-1225, 1305) * mm, "end": v(-1225, 1225) * mm});
            skLineSegment(sketch, "E77.bottom", {"start": v(1305, 1305) * mm, "end": v(1225, 1305) * mm});
            skLineSegment(sketch, "E77.top", {"start": v(1305, 1225) * mm, "end": v(1225, 1225) * mm});
            skLineSegment(sketch, "E77.left", {"start": v(1305, 1305) * mm, "end": v(1305, 1225) * mm});
            skLineSegment(sketch, "E77.right", {"start": v(1225, 1305) * mm, "end": v(1225, 1225) * mm});
            skLineSegment(sketch, "E78.bottom", {"start": v(1305, -1305) * mm, "end": v(1225, -1305) * mm});
            skLineSegment(sketch, "E78.top", {"start": v(1305, -1225) * mm, "end": v(1225, -1225) * mm});
            skLineSegment(sketch, "E78.left", {"start": v(1305, -1305) * mm, "end": v(1305, -1225) * mm});
            skLineSegment(sketch, "E78.right", {"start": v(1225, -1305) * mm, "end": v(1225, -1225) * mm});
            skLineSegment(sketch, "E79.bottom", {"start": v(-1305, -1305) * mm, "end": v(-1225, -1305) * mm});
            skLineSegment(sketch, "E79.top", {"start": v(-1305, -1225) * mm, "end": v(-1225, -1225) * mm});
            skLineSegment(sketch, "E79.left", {"start": v(-1305, -1305) * mm, "end": v(-1305, -1225) * mm});
            skLineSegment(sketch, "E79.right", {"start": v(-1225, -1305) * mm, "end": v(-1225, -1225) * mm});
            skSolve(sketch);
        }
        {
            var Q0;
            Q0=qSketchRegion(id+"F51",true);
            extrude(context, id + "F52", {"entities" : qUnion([Q0]), "operationType" : NewBodyOperationType.ADD, "depth" : 940 * mm});
        }
        {
            var Q0;
            Q0=makeQuery(id+"F52.boolean.opBoolean","MERGE",FACE,{"derivedFrom":[makeQuery(id+"F19.opPattern","COPY",FACE,{"derivedFrom":makeQuery(id+"F10.opExtrude","SWEPT_FACE",FACE,{"disambiguationData":[OSD([sQuery(id+"F9.wireOp",EDGE,"E3.top")])]}),"instanceName":"1"}),makeQuery(id+"F52.opExtrude","SWEPT_FACE",FACE,{"disambiguationData":[OSD([sQuery(id+"F51.wireOp",EDGE,"E76.bottom")])]}),makeQuery(id+"F52.opExtrude","SWEPT_FACE",FACE,{"disambiguationData":[OSD([sQuery(id+"F51.wireOp",EDGE,"E77.bottom")])]})]});
            var sketch = newSketch(context, id + "F53", { "sketchPlane" : qUnion([Q0])});
            skLineSegment(sketch, "E80", {"start": v(-743.2, -5) * mm, "end": v(-85, -945) * mm});
            skLineSegment(sketch, "E81", {"start": v(-85, -945) * mm, "end": v(-5, -945) * mm});
            skLineSegment(sketch, "E82", {"start": v(-5, -945) * mm, "end": v(-663.2, -5) * mm});
            skLineSegment(sketch, "E83", {"start": v(-663.2, -5) * mm, "end": v(-743.2, -5) * mm});
            skLineSegment(sketch, "E84.MirrorCS", {"start": v(5, -945) * mm, "end": v(663.2, -5) * mm});
            skLineSegment(sketch, "E85.MirrorCS", {"start": v(85, -945) * mm, "end": v(5, -945) * mm});
            skLineSegment(sketch, "E86.MirrorCS", {"start": v(743.2, -5) * mm, "end": v(85, -945) * mm});
            skLineSegment(sketch, "E87.MirrorCS", {"start": v(663.2, -5) * mm, "end": v(743.2, -5) * mm});
            skSolve(sketch);
        }
        {
            var Q0;
            Q0=qSketchRegion(id+"F53",true);
            var Q1;
            Q1=makeQuery(id+"F52.opExtrude","SWEPT_FACE",FACE,{"disambiguationData":[OSD([sQuery(id+"F51.wireOp",EDGE,"E76.top")])]});
            extrude(context, id + "F54", {"entities" : qUnion([Q0]), "endBound" : BoundingType.UP_TO_SURFACE, "oppositeDirection" : true, "endBoundEntityFace" : qUnion([Q1]), "depth" : 25 * mm});
        }
        {
            var Q0;
            Q0=makeQuery(id+"F54.opExtrude","SWEPT_BODY",BODY,{"disambiguationData":[OSD([sQuery(id+"F53.wireOp",EDGE,"E80"),sQuery(id+"F53.wireOp",EDGE,"E81"),sQuery(id+"F53.wireOp",EDGE,"E82"),sQuery(id+"F53.wireOp",EDGE,"E83")])]});
            var Q1;
            Q1=makeQuery(id+"F54.opExtrude","SWEPT_BODY",BODY,{"disambiguationData":[OSD([sQuery(id+"F53.wireOp",EDGE,"E84.MirrorCS"),sQuery(id+"F53.wireOp",EDGE,"E85.MirrorCS"),sQuery(id+"F53.wireOp",EDGE,"E86.MirrorCS"),sQuery(id+"F53.wireOp",EDGE,"E87.MirrorCS")])]});
            var Q2;
            Q2=qCreatedBy(makeId("Front.planeOp"),FACE);
            mirror(context, id + "F55", {"operationType" : NewBodyOperationType.ADD, "entities" : qUnion([Q0, Q1]), "mirrorPlane" : qUnion([Q2])});
        }
        {
            var Q0;
            Q0=makeQuery(id+"F52.boolean.opBoolean","MERGE",FACE,{"derivedFrom":[makeQuery(id+"F19.opPattern","COPY",FACE,{"derivedFrom":makeQuery(id+"F10.opExtrude","SWEPT_FACE",FACE,{"disambiguationData":[OSD([sQuery(id+"F9.wireOp",EDGE,"E3.left")])]}),"instanceName":"1"}),makeQuery(id+"F52.opExtrude","SWEPT_FACE",FACE,{"disambiguationData":[OSD([sQuery(id+"F51.wireOp",EDGE,"E76.left")])]}),makeQuery(id+"F52.opExtrude","SWEPT_FACE",FACE,{"disambiguationData":[OSD([sQuery(id+"F51.wireOp",EDGE,"E79.left")])]})]});
            var sketch = newSketch(context, id + "F56", { "sketchPlane" : qUnion([Q0])});
            skLineSegment(sketch, "E88", {"start": v(-743.2, -5) * mm, "end": v(-85, -945) * mm});
            skLineSegment(sketch, "E89", {"start": v(-85, -945) * mm, "end": v(-5, -945) * mm});
            skLineSegment(sketch, "E90", {"start": v(-5, -945) * mm, "end": v(-663.2, -5) * mm});
            skLineSegment(sketch, "E91", {"start": v(-663.2, -5) * mm, "end": v(-743.2, -5) * mm});
            skLineSegment(sketch, "E92.MirrorCS", {"start": v(85, -945) * mm, "end": v(5, -945) * mm});
            skLineSegment(sketch, "E93.MirrorCS", {"start": v(5, -945) * mm, "end": v(663.2, -5) * mm});
            skLineSegment(sketch, "E94.MirrorCS", {"start": v(743.2, -5) * mm, "end": v(85, -945) * mm});
            skLineSegment(sketch, "E95.MirrorCS", {"start": v(663.2, -5) * mm, "end": v(743.2, -5) * mm});
            skSolve(sketch);
        }
        {
            var Q0;
            Q0=qSketchRegion(id+"F56",true);
            var Q1;
            Q1=makeQuery(id+"F52.opExtrude","SWEPT_FACE",FACE,{"disambiguationData":[OSD([sQuery(id+"F51.wireOp",EDGE,"E79.right")])]});
            extrude(context, id + "F57", {"entities" : qUnion([Q0]), "endBound" : BoundingType.UP_TO_SURFACE, "oppositeDirection" : true, "endBoundEntityFace" : qUnion([Q1]), "depth" : 25 * mm});
        }
        {
            var Q0;
            Q0=makeQuery(id+"F57.opExtrude","SWEPT_BODY",BODY,{"disambiguationData":[OSD([sQuery(id+"F56.wireOp",EDGE,"E88"),sQuery(id+"F56.wireOp",EDGE,"E89"),sQuery(id+"F56.wireOp",EDGE,"E90"),sQuery(id+"F56.wireOp",EDGE,"E91")])]});
            var Q1;
            Q1=makeQuery(id+"F57.opExtrude","SWEPT_BODY",BODY,{"disambiguationData":[OSD([sQuery(id+"F56.wireOp",EDGE,"E92.MirrorCS"),sQuery(id+"F56.wireOp",EDGE,"E93.MirrorCS"),sQuery(id+"F56.wireOp",EDGE,"E94.MirrorCS"),sQuery(id+"F56.wireOp",EDGE,"E95.MirrorCS")])]});
            var Q2;
            Q2=qCreatedBy(makeId("Right.planeOp"),FACE);
            mirror(context, id + "F58", {"operationType" : NewBodyOperationType.ADD, "entities" : qUnion([Q0, Q1]), "mirrorPlane" : qUnion([Q2])});
        }
        {
            var Q0;
            Q0=makeQuery(id+"F19.opPattern","COPY",FACE,{"derivedFrom":makeQuery(id+"F10.opExtrude","CAP_FACE",FACE,{"disambiguationData":[OSD([sQuery(id+"F9.wireOp",EDGE,"E3.bottom"),sQuery(id+"F9.wireOp",EDGE,"E3.top"),sQuery(id+"F9.wireOp",EDGE,"E3.left"),sQuery(id+"F9.wireOp",EDGE,"E3.right"),sQuery(id+"F9.wireOp",EDGE,"E4.0"),sQuery(id+"F9.wireOp",EDGE,"E4.1"),sQuery(id+"F9.wireOp",EDGE,"E4.2"),sQuery(id+"F9.wireOp",EDGE,"E4.3")])],"isStart":true}),"instanceName":"1"});
            extrude(context, id + "F59", {"entities" : qUnion([Q0]), "operationType" : NewBodyOperationType.ADD, "oppositeDirection" : true, "depth" : 100 * mm});
        }
    });
